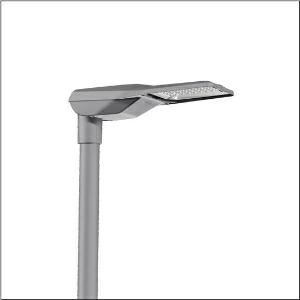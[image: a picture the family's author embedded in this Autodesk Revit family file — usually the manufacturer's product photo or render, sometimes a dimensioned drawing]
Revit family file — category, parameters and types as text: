
# Revit family: streetlight_sl_21_iq_mini___p1_0a_5xe2a31d08gb_969e
name_source: partatom
category: Lighting Fixtures
units: mm (PartAtom-declared; Revit-internal decimal feet)

## family parameters
Cut with Voids When Loaded = No
Host = Face
Light Source = No
Part Type = Normal
Room Calculation Point = No
Round Connector Dimension = Use Diameter
Shared = No

## types (1)
- --- (1 x LED, 5680 lm, 37.1 W, 3000K)
    Apparent Load = 37 VA
    CIE Flux Codes = 21 50 90 100 100
    Color Rendering = 70
    Color Temperature = 3000K
    Default Elevation = 1800 mm
    Description = Streetlight SL 21 iQ mini, mast luminaire, primary light control with lens, of PMMA, primary optical cover: cover, of toughened safety glass, transparent, light distribution: P1.0a, light emission: direct distribution, primary light characteristic: asymmetric, installation type: post-top, side-entry, LED, High Power LED, rated luminous flux: 5.680lm, luminous efficacy: 153lm/W, light colour: 730, colour temperature: 3000K, control: Auto-Match, Temp-Guard, Lumen-Switch, Night-Set, Smart-Wire, Light-Fading, Desk-Remote (wireless, voltage-free reading and setting of iQ features in the workshop via application-optimized NFC function/RFID function), optimised constant luminous flux control (CLO 2.0), presetting dimming linear, mains connection: 220..240V, AC, 50/60Hz, start of lifetime: 37W, end of service life: 39W, reduction: 18W, luminaire housing, of diecast aluminium, powder-coated, Siteco® metallic grey (DB 702S), corrosivity category C5 mid according to DIN EN ISO 12944, please order mast flange separately, inclination adjustable: 0°, 5°, 10°, 15°, sealing non-destructively replaceable, multi-level sealing system, length: 628mm, width: 235mm, height: 110mm, mast flange for spigot size: 42mm (side-entry): 5XC10008XM4, 60/48mm (side-entry/post-top): 5XC10108XM2, 76/60mm (side-entry/post-top): 5XC10108XM1, protection rating (complete): IP66, insulation class (complete): insulation class II (safety insulation), certification: CE, ENEC, ENEC+, VDE, impact resistance: IK09, permissible operating ambient temperature for outdoor applications: -40..+50°C, standard-compliant lighting for roads and squares, packaging unit: 1 piece

Light Distribution: P1.0a
    Height = 110 mm
    Lamp = 1 x LED
    Lamp Light Flux = 5680 lm
    Lamp Power = 37.1 W
    Lamp count = 1
    Length = 625 mm
    Luminous efficacy = 153 lm/W
    Manufacturer = Siteco
    ModVariant = No
    Model = 5XE2A31D08GB
    Number of Poles = 1
    OnlyDefault = Yes
    Power Factor = 1
    Product Name = Streetlight SL 21 iQ mini | P1.0a
    Product group = mast luminaire | pylon top
    ProductGroupID = 6100
    Protection Class = Protection class II
    Protection Degree = IP 66
    RLX_Detail_Level = 1
    RLX_Emergency_Light_Flux = 0 lm
    RLX_Emergency_Type = 0
    RLX_Emergency_Type_DB = No
    RlxData = <blob elided: 103529 chars, md5=5a830bf5>
    Socket = socket
    Standby Power = 0 W
    System Light Flux = 5680 lm
    System Power = 37 W
    Type Comments = factory setting: luminous flux: 100 % | dim-lin: 254 | 385 mA
    Type Image = l_1003519.jpg
    URL = http://relux.com
    VarID = @adj_138683
    Voltage = 0 V
    Weight = 0.00 kg
    Width = 234 mm

## geometry (parser evidence)
native form markers: Blend x4, Sweep x8
no freeform markers — native parametric forms only
